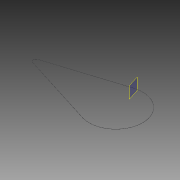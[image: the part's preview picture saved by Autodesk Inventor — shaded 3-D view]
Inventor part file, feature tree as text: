
AUTODESK INVENTOR PART (.ipt)
format: ipt  version: 2013 (Build 170138000, 138)  size: 82,944 bytes
history: native  units: mm
features: sketch x2, plane x1, sweep x1
ambient origin geometry x8: Origin, YZ Plane, XZ Plane, XY Plane, X Axis, Y Axis, Z Axis, Center Point
bodies: Solid1 (feature_tree)
feature tree (4):
  sketch  "Sketch1"  dims[d0=150.0mm d1=10.25mm]
  plane  "Work Plane1"
  sweep  "Sweep1"
  sketch  "Sketch2"  dims[d2=100.25mm d3=0.5mm d5=0.0mm]
